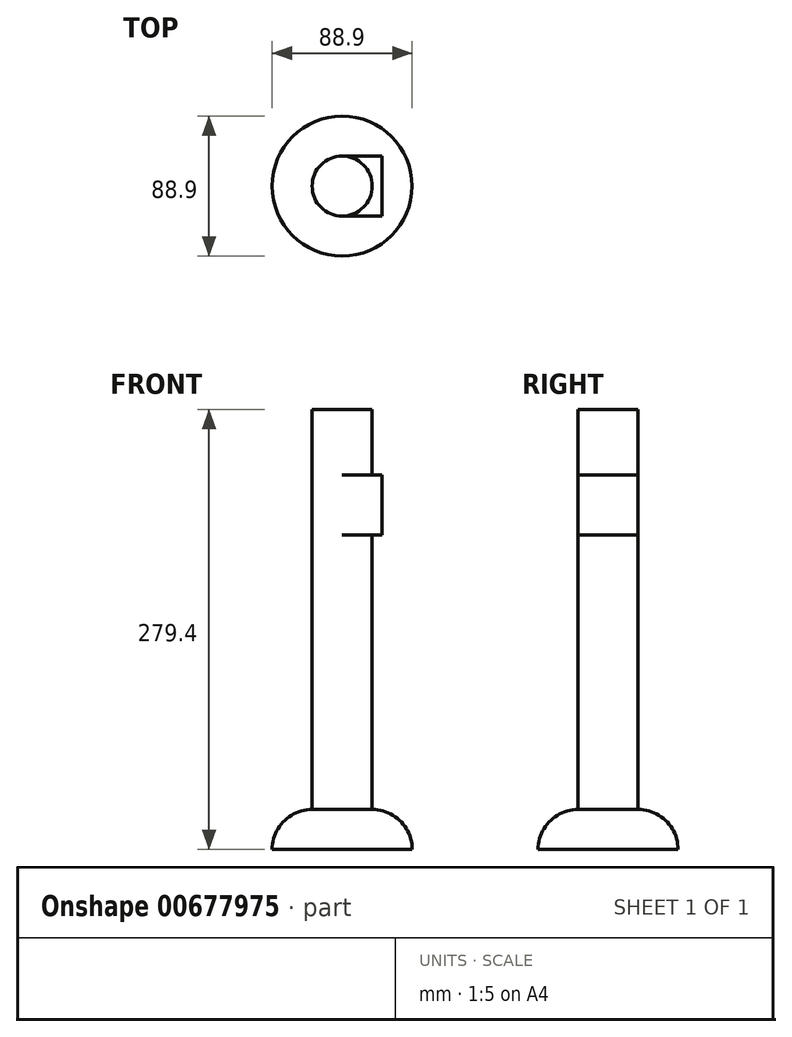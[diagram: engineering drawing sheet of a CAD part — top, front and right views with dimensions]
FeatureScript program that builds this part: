
annotation { "Feature Type Name" : "Feature", "Feature Type Description" : "" }
export const myFeature = defineFeature(function(context is Context, id is Id, definition is map)
    precondition{}
    {
        {
            var Q0;
            Q0=qCreatedBy(makeId("Top.planeOp"),FACE);
            var sketch = newSketch(context, id + "F0", { "sketchPlane" : qUnion([Q0])});
            skCircle(sketch, "E0", {"center": v(0, 0) * mm, "radius": 44.45 * mm});
            skSolve(sketch);
        }
        {
            var Q0;
            Q0=makeQuery(id+"F0.imprint","IMPRINT",FACE,{"disambiguationData":[TD([[makeQuery(id+"F0.imprint","IMPRINT",EDGE,{"derivedFrom":sQuery(id+"F0.wireOp",EDGE,"E0")}),1.0]])]});
            extrude(context, id + "F1", {"entities" : qUnion([Q0]), "depth" : 25.4 * mm, "offsetDistance" : 25.4 * mm});
        }
        {
            var Q0;
            Q0=makeQuery(id+"F1.opExtrude","CAP_EDGE",EDGE,{"disambiguationData":[OSD([sQuery(id+"F0.wireOp",EDGE,"E0")])],"isStart":false});
            fillet(context, id + "F2", {"entities" : qUnion([Q0]), "radius" : 25.4 * mm, "tangentPropagation" : true, "allowEdgeOverflow" : false});
        }
        {
            var Q0;
            Q0=makeQuery(id+"F1.opExtrude","CAP_FACE",FACE,{"disambiguationData":[OSD([sQuery(id+"F0.wireOp",EDGE,"E0")])],"isStart":false});
            extrude(context, id + "F3", {"entities" : qUnion([Q0]), "operationType" : NewBodyOperationType.ADD, "depth" : 254 * mm, "offsetDistance" : 25.4 * mm});
        }
        {
            var Q0;
            Q0=qCreatedBy(makeId("Right.planeOp"),FACE);
            var sketch = newSketch(context, id + "F4", { "sketchPlane" : qUnion([Q0])});
            skLineSegment(sketch, "E1.bottom", {"start": v(-19.05, 199.8) * mm, "end": v(19.05, 199.8) * mm});
            skLineSegment(sketch, "E1.top", {"start": v(-19.05, 237.9) * mm, "end": v(19.05, 237.9) * mm});
            skLineSegment(sketch, "E1.left", {"start": v(-19.05, 199.8) * mm, "end": v(-19.05, 237.9) * mm});
            skLineSegment(sketch, "E1.right", {"start": v(19.05, 199.8) * mm, "end": v(19.05, 237.9) * mm});
            skPoint(sketch, "E1.middle", {"position": v(0, 218.84) * mm});
            skSolve(sketch);
        }
        {
            var Q0;
            Q0 = qSketchRegion(id + "F4", true);
            extrude(context, id + "F5", {"entities" : qUnion([Q0]), "operationType" : NewBodyOperationType.ADD, "depth" : 25.4 * mm, "offsetDistance" : 25.4 * mm});
        }
    });
